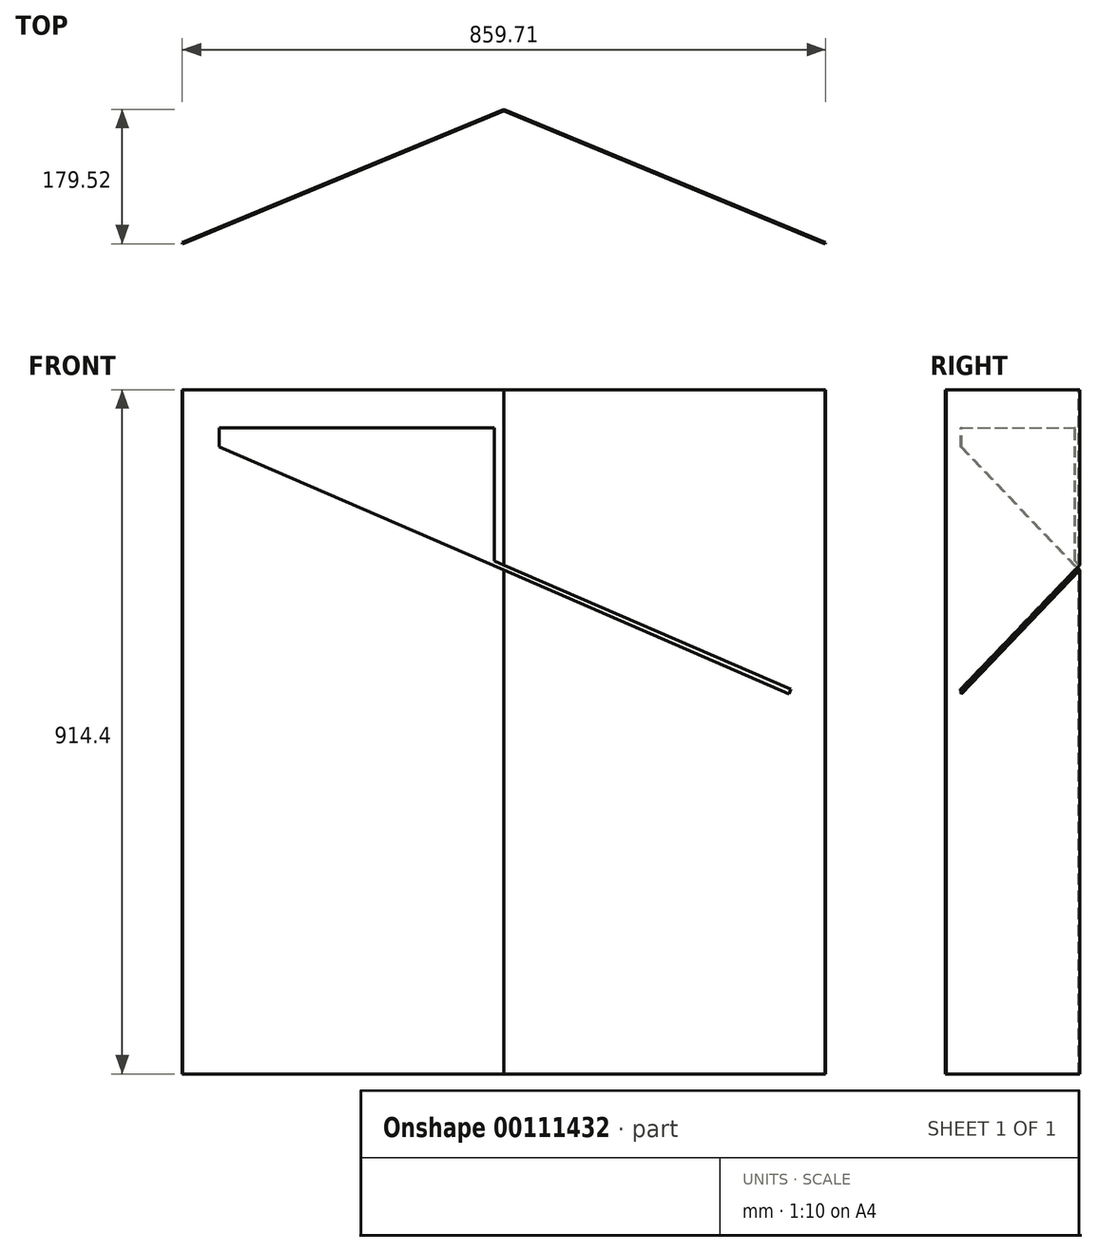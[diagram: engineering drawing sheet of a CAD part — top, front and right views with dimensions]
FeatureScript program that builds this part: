
annotation { "Feature Type Name" : "Feature", "Feature Type Description" : "" }
export const myFeature = defineFeature(function(context is Context, id is Id, definition is map)
    precondition{}
    {
        {
            var Q0;
            Q0=qCreatedBy(makeId("Top.planeOp"),FACE);
            var sketch = newSketch(context, id + "F0", { "sketchPlane" : qUnion([Q0])});
            skLineSegment(sketch, "E0", {"start": v(0, 0) * mm, "end": v(429.25, 177.8) * mm});
            skLineSegment(sketch, "E1", {"start": v(429.25, 177.8) * mm, "end": v(858.5, 0) * mm});
            skLineSegment(sketch, "E2.0", {"start": v(429.25, 179.52) * mm, "end": v(859.1, 1.47) * mm});
            skLineSegment(sketch, "E2.1", {"start": v(-0.6, 1.47) * mm, "end": v(429.25, 179.52) * mm});
            skLineSegment(sketch, "E3", {"start": v(-0.6, 1.47) * mm, "end": v(0, 0) * mm});
            skLineSegment(sketch, "E4", {"start": v(858.5, 0) * mm, "end": v(859.1, 1.47) * mm});
            skSolve(sketch);
        }
        {
            var Q0;
            Q0 = qSketchRegion(id + "F0", true);
            extrude(context, id + "F1", {"entities" : qUnion([Q0]), "oppositeDirection" : true, "depth" : 914.4 * mm});
        }
        {
            var Q0;
            Q0=makeQuery(id+"F1.opExtrude","SWEPT_EDGE",EDGE,{"disambiguationData":[OSD([sQuery(id+"F0.wireOp",EDGE,"E2.1"),sQuery(id+"F0.wireOp",EDGE,"E3")])]});
            var Q1;
            Q1=makeQuery(id+"F1.opExtrude","SWEPT_EDGE",EDGE,{"disambiguationData":[OSD([sQuery(id+"F0.wireOp",EDGE,"E2.0"),sQuery(id+"F0.wireOp",EDGE,"E4")])]});
            cPlane(context, id + "F2", {"entities" : qUnion([Q0, Q1]), "cplaneType" : CPlaneType.LINE_ANGLE, "offset" : 25.4 * mm, "angle" : 0 * degree, "width" : 152.4 * mm, "height" : 152.4 * mm});
        }
        {
            var Q0;
            Q0=qCreatedBy(id+"F2.planeOp",FACE);
            var sketch = newSketch(context, id + "F3", { "sketchPlane" : qUnion([Q0])});
            skLineSegment(sketch, "E5", {"start": v(-48.94, -76.2) * mm, "end": v(-810.16, -406.4) * mm});
            skLineSegment(sketch, "E6", {"start": v(-48.94, -76.2) * mm, "end": v(-48.94, -50.8) * mm});
            skLineSegment(sketch, "E7", {"start": v(-416.23, -228.6) * mm, "end": v(-416.23, -50.8) * mm});
            skLineSegment(sketch, "E8", {"start": v(-810.16, -406.4) * mm, "end": v(-812.69, -400.57) * mm});
            skLineSegment(sketch, "E9", {"start": v(-812.69, -400.57) * mm, "end": v(-416.23, -228.6) * mm});
            skLineSegment(sketch, "E10", {"start": v(-48.94, -50.8) * mm, "end": v(-416.23, -50.8) * mm});
            skSolve(sketch);
        }
        {
            var Q0;
            Q0 = qSketchRegion(id + "F3", true);
            extrude(context, id + "F4", {"entities" : qUnion([Q0]), "operationType" : NewBodyOperationType.REMOVE, "endBound" : BoundingType.THROUGH_ALL, "depth" : 25.4 * mm});
        }
    });
